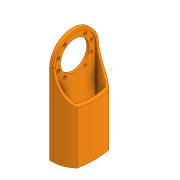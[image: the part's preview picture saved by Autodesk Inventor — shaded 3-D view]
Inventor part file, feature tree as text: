
AUTODESK INVENTOR PART (.ipt)
format: ipt  version: 2020 (Build 240168000, 168)  size: 243,200 bytes
history: native  units: in
note: dims shown in document units (in); Inventor stores cm internally (conversion verified against a paired STEP export)
features: sketch x9, extrude x7, projected_geometry x1
ambient origin geometry x8: Origin, YZ Plane, XZ Plane, XY Plane, X Axis, Y Axis, Z Axis, Center Point
bodies: Solid1 (feature_tree)
feature tree (17):
  extrude  "Extrusion1"  Depth=0.2362in
  sketch  "Sketch2"  dims[d6=0.2362in d7=0.2362in]
  extrude  "Extrusion2"  Depth=0.2362in
  sketch  "Sketch4"  dims[d10=0.2362in d11=0.2362in]
  extrude  "Extrusion3"  Depth=0.2362in
  extrude  "Extrusion4"  Depth=0.2362in
  extrude  "Extrusion5"  Depth=0.2362in
  extrude  "Extrusion6"  Depth=0.0394in
  extrude  "Extrusion7"  Depth=0.1969in
  sketch  "Sketch1"  dims[d3=2.3622in d5=0.2362in]
  sketch  "Sketch3"  dims[d8=0.2362in d9=0.2362in]
  sketch  "Sketch5"  dims[d12=0.2362in d13=4.85in]
  sketch  "Sketch6"  dims[d14=0.1969in d15=0.0in d16=0.0394in]
  projected_geometry  "Projected Loop1"
  sketch  "Sketch8"  dims[d17=0.0394in d18=0.1969in]
  sketch  "Sketch9"  dims[d19=0.1969in]
  sketch  "Sketch10"  dims[d20=0.0787in d21=0.0in d22=1.7717in d23=1.2598in d24=2.5197in d25=0.1181in d26=0.1969in d27=6.4173in d28=0.0in d29=1.1811in d30=6.4173in d31=0.0in d32=1.6732in d33=0.5906in d34=0.5906in d35=0.2717in d36=0.2717in d37=0.315in d38=0.0in d39=0.4724in d40=0.4724in d41=0.1181in d42=0.0in d43=0.1181in d44=0.0in]
